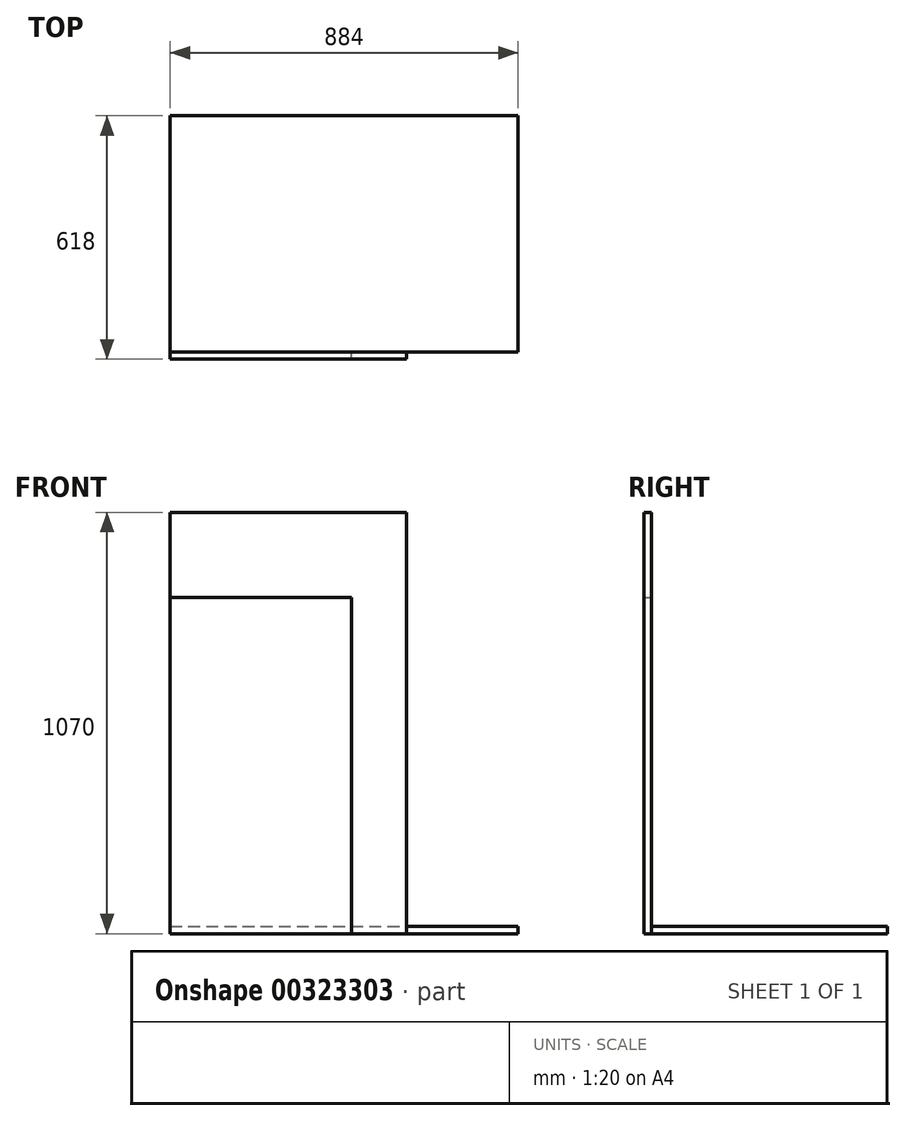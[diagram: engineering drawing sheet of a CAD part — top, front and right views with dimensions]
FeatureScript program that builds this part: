
annotation { "Feature Type Name" : "Feature", "Feature Type Description" : "" }
export const myFeature = defineFeature(function(context is Context, id is Id, definition is map)
    precondition{}
    {
        {
            var Q0;
            Q0=qCreatedBy(makeId("Top.planeOp"),FACE);
            var sketch = newSketch(context, id + "F0", { "sketchPlane" : qUnion([Q0])});
            skLineSegment(sketch, "E0.bottom", {"start": v(0, 0) * mm, "end": v(884, 0) * mm});
            skLineSegment(sketch, "E0.top", {"start": v(0, 600) * mm, "end": v(884, 600) * mm});
            skLineSegment(sketch, "E0.left", {"start": v(0, 0) * mm, "end": v(0, 600) * mm});
            skLineSegment(sketch, "E0.right", {"start": v(884, 0) * mm, "end": v(884, 600) * mm});
            skSolve(sketch);
        }
        {
            var Q0;
            Q0 = qSketchRegion(id + "F0", true);
            extrude(context, id + "F1", {"entities" : qUnion([Q0]), "depth" : 18 * mm, "offsetDistance" : 25 * mm});
        }
        {
            var Q0;
            Q0=qCreatedBy(makeId("Front.planeOp"), FACE);
            var sketch = newSketch(context, id + "F2", { "sketchPlane" : qUnion([Q0])});
            skLineSegment(sketch, "E1.bottom", {"start": v(0, 0) * mm, "end": v(600, 0) * mm});
            skLineSegment(sketch, "E1.top", {"start": v(0, 1070) * mm, "end": v(600, 1070) * mm});
            skLineSegment(sketch, "E1.left", {"start": v(0, 0) * mm, "end": v(0, 1070) * mm});
            skLineSegment(sketch, "E1.right", {"start": v(600, 0) * mm, "end": v(600, 1070) * mm});
            skSolve(sketch);
        }
        {
            var Q0;
            Q0 = qSketchRegion(id + "F2", true);
            extrude(context, id + "F3", {"entities" : qUnion([Q0]), "domain" : OperationDomain.MODEL, "flatOperationType" : FlatOperationType.REMOVE, "depth" : 18 * mm, "offsetDistance" : 25 * mm});
        }
        {
            var Q0;
            Q0=qCreatedBy(makeId("Front.planeOp"), FACE);
            var sketch = newSketch(context, id + "F4", { "sketchPlane" : qUnion([Q0])});
            skLineSegment(sketch, "E2.bottom", {"start": v(0, 0) * mm, "end": v(460, 0) * mm});
            skLineSegment(sketch, "E2.top", {"start": v(0, 854) * mm, "end": v(460, 854) * mm});
            skLineSegment(sketch, "E2.left", {"start": v(0, 0) * mm, "end": v(0, 854) * mm});
            skLineSegment(sketch, "E2.right", {"start": v(460, 0) * mm, "end": v(460, 854) * mm});
            skSolve(sketch);
        }
        {
            var Q0;
            Q0 = qSketchRegion(id + "F4", true);
            extrude(context, id + "F5", {"entities" : qUnion([Q0]), "domain" : OperationDomain.MODEL, "flatOperationType" : FlatOperationType.REMOVE, "depth" : 18 * mm, "offsetDistance" : 25 * mm});
        }
    });
